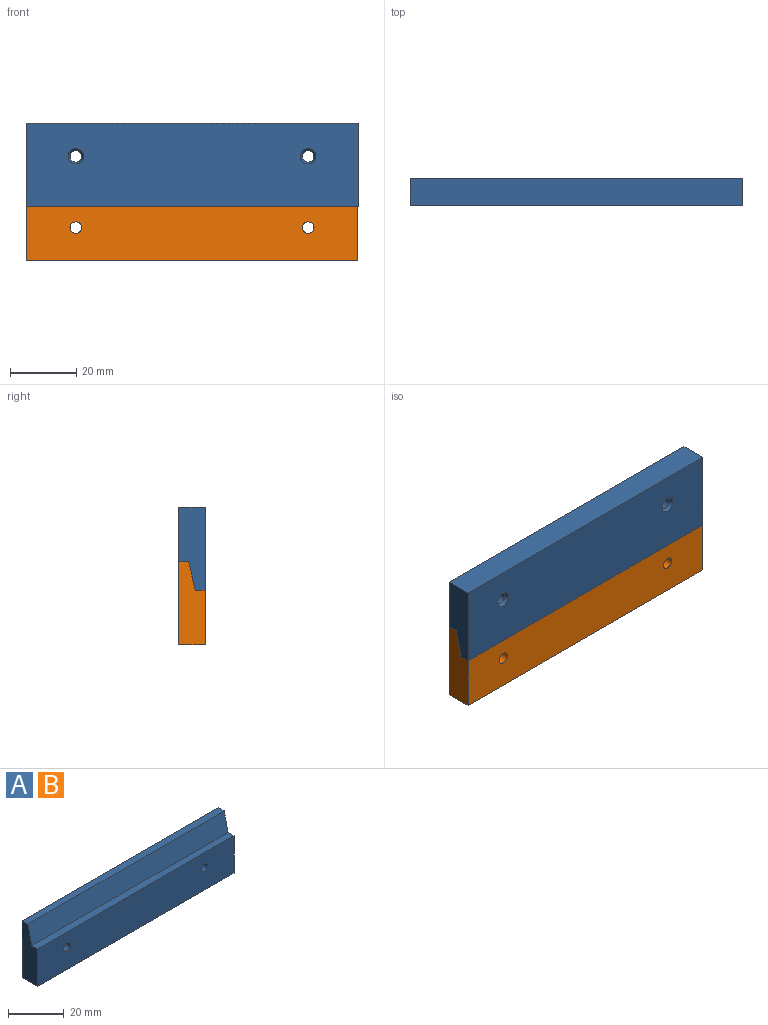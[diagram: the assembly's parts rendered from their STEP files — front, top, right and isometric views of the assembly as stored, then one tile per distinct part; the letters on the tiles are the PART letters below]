
ASSEMBLY  parts=2 mates=1
PART A: 12 faces, bbox 100x8x25 mm
  f0: plane 100x25mm, normal (0,1,0), area 2466mm2, adj f1,f5,f6,f7,f10,f11
  f1: plane 100x3mm, normal (0,0,1), area 300mm2, adj f0,f2,f6,f7
  f2: plane 100x8.5mm, normal (0,-0.97,0.23), area 873.2mm2, adj f1,f3,f6,f7
  f3: plane 100x3mm, normal (0,0,1), area 300mm2, adj f2,f4,f6,f7
  f4: plane 100x16.5mm, normal (0,-1,0), area 1630.8mm2, adj f3,f5,f6,f7,f8,f9
  f5: plane 100x8mm, normal (0,0,-1), area 800mm2, adj f0,f4,f6,f7
  f6: plane 25x8mm, normal (1,0,0), area 166mm2, adj f0,f1,f2,f3,f4,f5
  f7: plane 25x8mm, normal (-1,0,0), area 166mm2, adj f0,f1,f2,f3,f4,f5
  f8: cylinder r=1.75mm len=7mm, axis (0,1,0), area 77mm2, adj f4,f10
  f9: cylinder r=1.75mm len=7mm, axis (0,1,0), area 77mm2, adj f4,f11
  f10: cone r=1.75mm half-angle=30deg, axis (0,1,0), area 14.8mm2, adj f0,f8
  f11: cone r=1.75mm half-angle=30deg, axis (0,1,0), area 14.8mm2, adj f0,f9
PART B: same geometry as A
PLACE A rot(axis=(1,0,0),180deg) t=(42.44,-0.18,8.62)mm
PLACE B t=(42.44,-0.18,-7.88)mm
MATE fastened A.f2 <-> B.f2  axis (0,0.97,-0.23) through (-7.56,-0.18,0.37)mm
